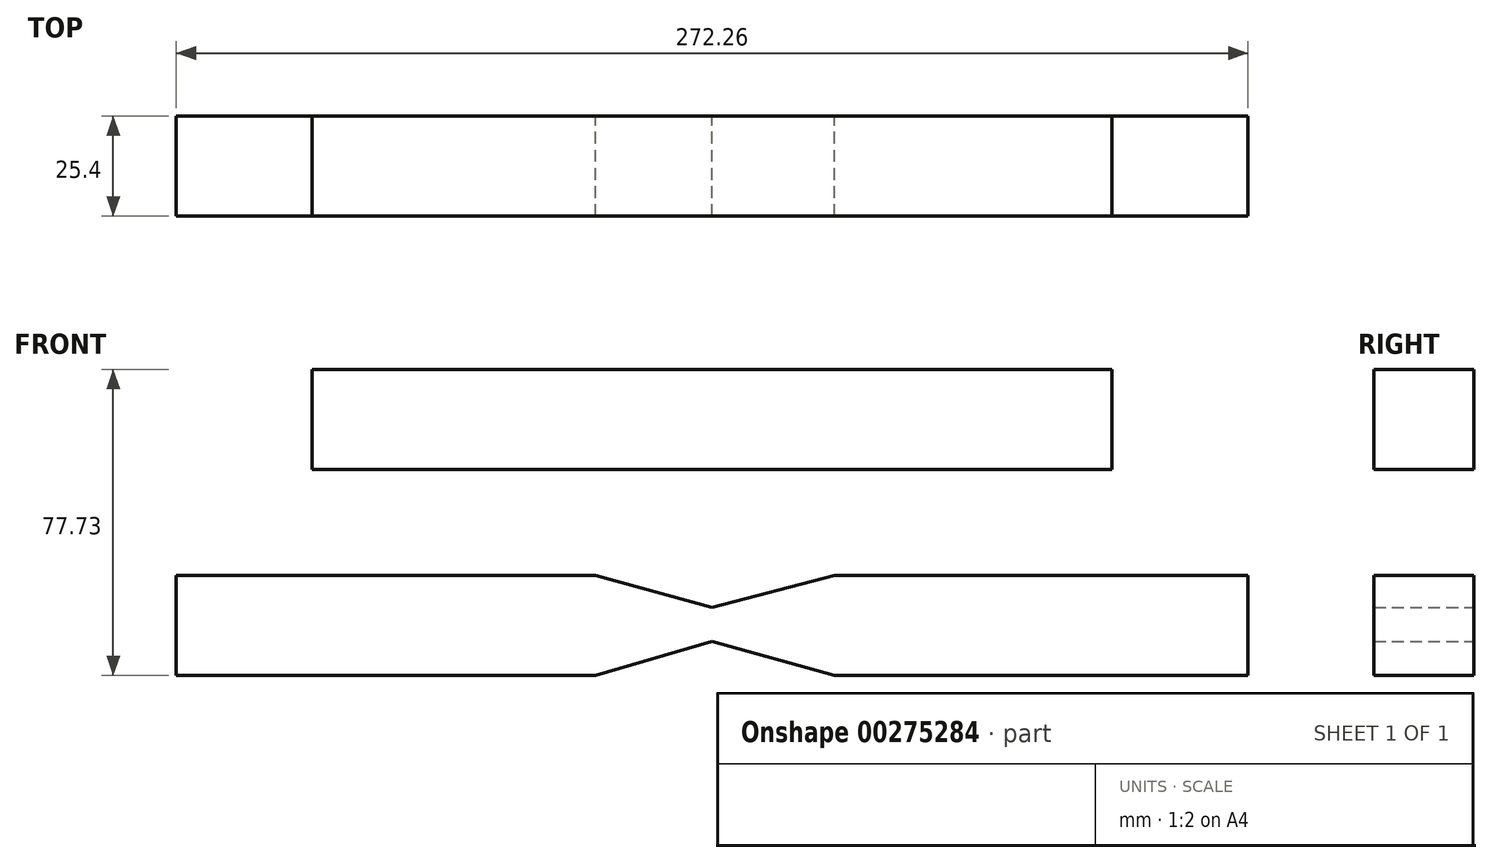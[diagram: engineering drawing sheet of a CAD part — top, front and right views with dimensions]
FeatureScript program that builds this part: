
annotation { "Feature Type Name" : "Feature", "Feature Type Description" : "" }
export const myFeature = defineFeature(function(context is Context, id is Id, definition is map)
    precondition{}
    {
        {
            var Q0;
            Q0=qCreatedBy(makeId("Front.planeOp"),FACE);
            var sketch = newSketch(context, id + "F0", { "sketchPlane" : qUnion([Q0])});
            skLineSegment(sketch, "E0.bottom", {"start": v(-101.6, 16.93) * mm, "end": v(101.6, 16.93) * mm});
            skLineSegment(sketch, "E0.top", {"start": v(-101.6, 42.33) * mm, "end": v(101.6, 42.33) * mm});
            skLineSegment(sketch, "E0.left", {"start": v(-101.6, 16.93) * mm, "end": v(-101.6, 42.33) * mm});
            skLineSegment(sketch, "E0.right", {"start": v(101.6, 16.93) * mm, "end": v(101.6, 42.33) * mm});
            skPoint(sketch, "E0.middle", {"position": v(0, 29.63) * mm});
            skLineSegment(sketch, "E1.bottom", {"start": v(-136.13, -35.4) * mm, "end": v(136.13, -35.4) * mm});
            skLineSegment(sketch, "E1.top", {"start": v(-136.13, -10) * mm, "end": v(136.13, -10) * mm});
            skLineSegment(sketch, "E1.left", {"start": v(-136.13, -35.4) * mm, "end": v(-136.13, -10) * mm});
            skLineSegment(sketch, "E1.right", {"start": v(136.13, -35.4) * mm, "end": v(136.13, -10) * mm});
            skPoint(sketch, "E1.middle", {"position": v(0, -22.7) * mm});
            skLineSegment(sketch, "E2", {"start": v(-29.64, -10) * mm, "end": v(0, -18.13) * mm});
            skLineSegment(sketch, "E3", {"start": v(-29.64, -35.4) * mm, "end": v(0, -26.77) * mm});
            skLineSegment(sketch, "E4", {"start": v(0, -26.77) * mm, "end": v(31.08, -35.4) * mm});
            skLineSegment(sketch, "E5", {"start": v(31.08, -10) * mm, "end": v(0, -18.13) * mm});
            skLineSegment(sketch, "E6", {"start": v(-78.71, 42.33) * mm, "end": v(-78.71, 16.93) * mm});
            skLineSegment(sketch, "E7", {"start": v(76.99, 42.33) * mm, "end": v(76.99, 16.93) * mm});
            skLineSegment(sketch, "E8", {"start": v(-119.3, -10) * mm, "end": v(-119.3, -35.4) * mm});
            skLineSegment(sketch, "E9", {"start": v(117.57, -10) * mm, "end": v(117.57, -35.4) * mm});
            skSolve(sketch);
        }
        {
            var Q0;
            Q0=makeQuery(id+"F0.imprint","IMPRINT",FACE,{"disambiguationData":[TD([[makeQuery(id+"F0.imprint","IMPRINT",EDGE,{"derivedFrom":sQuery(id+"F0.wireOp",EDGE,"E0.bottom")}),1.0]])]});
            var Q1;
            {var subQ3=sQuery(id+"F0.wireOp",EDGE,"E1.left");Q1=makeQuery(id+"F0.imprint","IMPRINT",FACE,{"disambiguationData":[TD([[makeQuery(id+"F0.imprint","IMPRINT",EDGE,{"derivedFrom":subQ3}),-1.0]])]});}
            var Q2;
            {var subQ3=sQuery(id+"F0.wireOp",EDGE,"E2");Q2=makeQuery(id+"F0.imprint","IMPRINT",FACE,{"disambiguationData":[TD([[makeQuery(id+"F0.imprint","IMPRINT",EDGE,{"derivedFrom":subQ3}),-1.0]])]});}
            var Q3;
            {var subQ0=sQuery(id+"F0.wireOp",EDGE,"E1.right");Q3=makeQuery(id+"F0.imprint","IMPRINT",FACE,{"disambiguationData":[TD([[makeQuery(id+"F0.imprint","IMPRINT",EDGE,{"derivedFrom":subQ0}),1.0]])]});}
            extrude(context, id + "F1", {"entities" : qUnion([Q0, Q1, Q2, Q3]), "depth" : 25.4 * mm});
        }
    });
